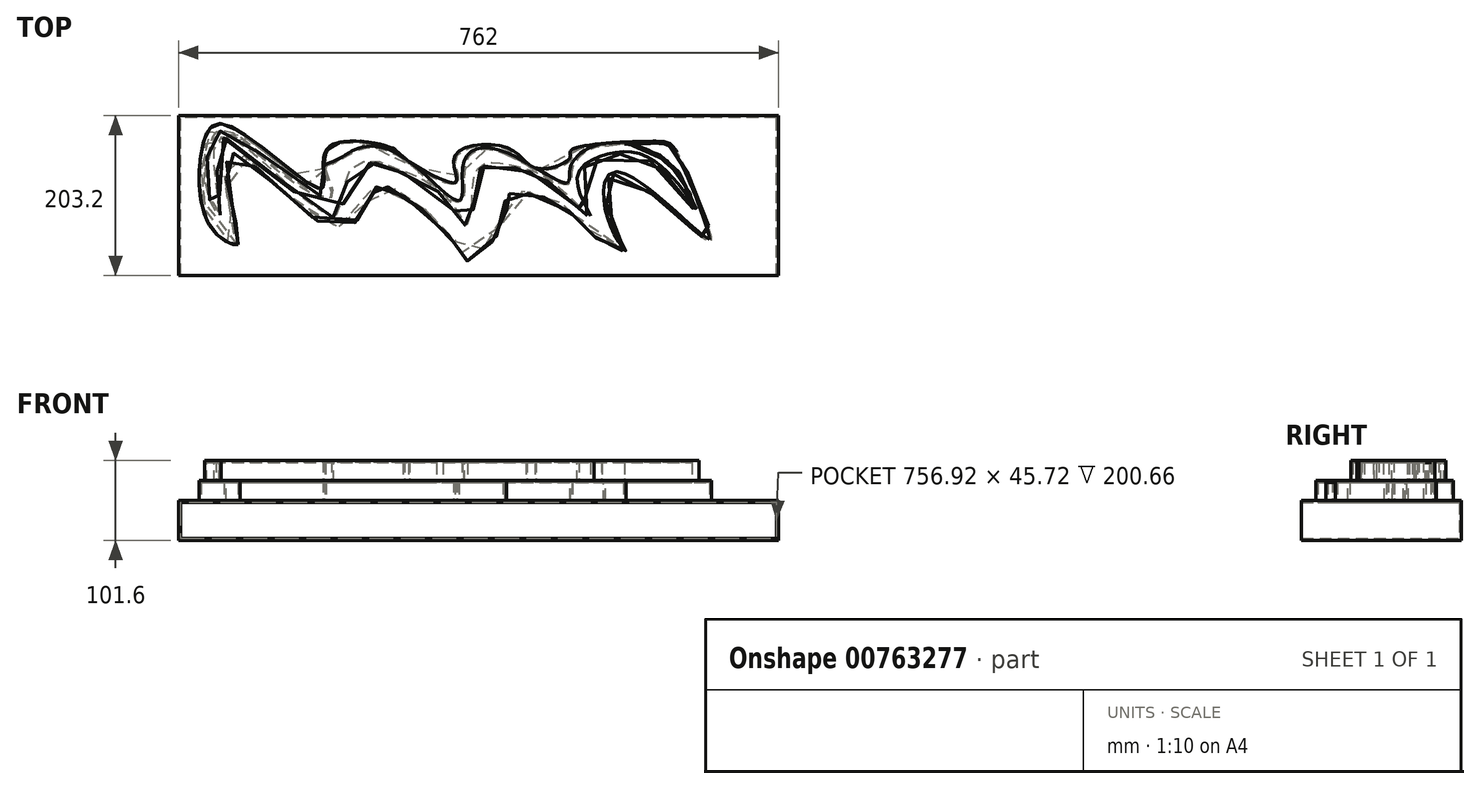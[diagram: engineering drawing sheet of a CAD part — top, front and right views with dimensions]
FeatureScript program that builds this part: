
annotation { "Feature Type Name" : "Feature", "Feature Type Description" : "" }
export const myFeature = defineFeature(function(context is Context, id is Id, definition is map)
    precondition{}
    {
        {
            var Q0;
            Q0=qCreatedBy(makeId("Front.planeOp"),FACE);
            var sketch = newSketch(context, id + "F0", { "sketchPlane" : qUnion([Q0])});
            skLineSegment(sketch, "E0.bottom", {"start": v(435.44, 50.8) * mm, "end": v(-326.56, 50.8) * mm});
            skLineSegment(sketch, "E0.top", {"start": v(435.44, 0) * mm, "end": v(-326.56, 0) * mm});
            skLineSegment(sketch, "E0.left", {"start": v(435.44, 50.8) * mm, "end": v(435.44, 0) * mm});
            skLineSegment(sketch, "E0.right", {"start": v(-326.56, 50.8) * mm, "end": v(-326.56, 0) * mm});
            skSolve(sketch);
        }
        {
            var Q0;
            Q0=makeQuery(id+"F0.imprint","IMPRINT",FACE,{"disambiguationData":[TD([[makeQuery(id+"F0.imprint","IMPRINT",EDGE,{"derivedFrom":sQuery(id+"F0.wireOp",EDGE,"E0.bottom")}),1.0]])]});
            extrude(context, id + "F1", {"entities" : qUnion([Q0]), "depth" : 203.2 * mm, "offsetDistance" : 25.4 * mm});
        }
        {
            var Q0;
            Q0=makeQuery(id+"F1.opExtrude","SWEPT_FACE",FACE,{"disambiguationData":[OSD([sQuery(id+"F0.wireOp",EDGE,"E0.bottom")])]});
            var sketch = newSketch(context, id + "F2", { "sketchPlane" : qUnion([Q0])});
            skFitSpline(sketch, "E1", {"points": [v(-250.77, -163.82) * mm, v(-255.18, -132) * mm, v(-258.15, -47.84) * mm, v(-124.06, -144.34) * mm, v(-77.46, -94.9) * mm, v(-66.59, -88.61) * mm, v(19.98, -156.73) * mm, v(42.07, -184.77) * mm, v(89.1, -128.63) * mm, v(89.96, -101.3) * mm, v(153.83, -110.58) * mm, v(200.1, -152.58) * mm, v(241.23, -171.78) * mm, v(224.31, -139.68) * mm, v(228.69, -73.8) * mm, v(347.16, -160) * mm, v(348.49, -147.43) * mm, v(304.78, -43.83) * mm, v(277.46, -32.77) * mm, v(171.93, -44.3) * mm, v(170.42, -53.77) * mm, v(128.73, -67.1) * mm, v(91.77, -41.2) * mm, v(23.32, -52.81) * mm, v(25.65, -84.74) * mm, v(-39.93, -53.9) * mm, v(-56.54, -40.94) * mm, v(-138.46, -43.15) * mm, v(-144.64, -92.88) * mm, v(-267.42, -11.32) * mm, v(-296.19, -38.66) * mm, v(-285.8, -142.18) * mm, v(-250.77, -163.82) * mm]});
            skSolve(sketch);
        }
        {
            var Q0;
            Q0=makeQuery(id+"F2.imprint","IMPRINT",FACE,{"disambiguationData":[TD([[makeQuery(id+"F2.imprint","IMPRINT",EDGE,{"derivedFrom":sQuery(id+"F2.wireOp",EDGE,"E1")}),1.0]])]});
            extrude(context, id + "F3", {"entities" : qUnion([Q0]), "operationType" : NewBodyOperationType.ADD, "depth" : 25.4 * mm, "offsetDistance" : 25.4 * mm});
        }
        {
            var Q0;
            Q0=makeQuery(id+"F3.opExtrude","CAP_FACE",FACE,{"disambiguationData":[OSD([sQuery(id+"F2.wireOp",EDGE,"E1")])],"isStart":false});
            var sketch = newSketch(context, id + "F4", { "sketchPlane" : qUnion([Q0])});
            skFitSpline(sketch, "E2", {"points": [v(-273.64, -126.3) * mm, v(-278.73, -43.22) * mm, v(-260.7, -30.87) * mm, v(-127.55, -129.53) * mm, v(-107.33, -70.92) * mm, v(-69.71, -61.74) * mm, v(-55.65, -67.6) * mm, v(6.06, -99.74) * mm, v(40.46, -140.71) * mm, v(48.82, -103.91) * mm, v(58.82, -65.47) * mm, v(104.04, -67.18) * mm, v(150.79, -90.11) * mm, v(200.7, -132.64) * mm, v(182.06, -84.44) * mm, v(204.26, -56.55) * mm, v(265.44, -53.69) * mm, v(325.36, -116.07) * mm, v(334.27, -129.9) * mm, v(314.92, -81) * mm, v(299.8, -63.41) * mm, v(273.46, -42.82) * mm, v(210.57, -35.77) * mm, v(171.23, -65.4) * mm, v(166.74, -85.54) * mm, v(81.7, -44.01) * mm, v(36.08, -58.34) * mm, v(30.62, -107.89) * mm, v(-39.77, -54.03) * mm, v(-98, -41.67) * mm, v(-130.45, -58.48) * mm, v(-142.84, -66.5) * mm, v(-132.52, -103.22) * mm, v(-200.43, -67.32) * mm, v(-257.08, -23) * mm, v(-280.25, -21.99) * mm, v(-286.25, -36.52) * mm, v(-293.04, -67.49) * mm, v(-286.52, -109.32) * mm, v(-273.64, -126.3) * mm]});
            skSolve(sketch);
        }
        {
            var Q0;
            {var subQ0=sQuery(id+"F4.wireOp",EDGE,"E2");var subQ1=makeQuery(id+"F3.opExtrude","CAP_EDGE",EDGE,{"disambiguationData":[OSD([sQuery(id+"F2.wireOp",EDGE,"E1")])],"isStart":false});var subQ8=makeQuery(id+"F4.imprint","INTERSECT",VERTEX,{"disambiguationData":[OD(0.0)],"derivedFrom":[subQ1,subQ0]});Q0=makeQuery(id+"F4.imprint","IMPRINT",FACE,{"disambiguationData":[TD([[makeQuery(id+"F4.imprint","IMPRINT",EDGE,{"disambiguationData":[TD([[subQ8,-1.0]])],"derivedFrom":subQ0}),1.0]])]});}
            extrude(context, id + "F5", {"entities" : qUnion([Q0]), "operationType" : NewBodyOperationType.ADD, "depth" : 25.4 * mm, "offsetDistance" : 25.4 * mm});
        }
        {
            var Q0;
            Q0=makeQuery(id+"F1.opExtrude","CAP_FACE",FACE,{"disambiguationData":[OSD([sQuery(id+"F0.wireOp",EDGE,"E0.bottom"),sQuery(id+"F0.wireOp",EDGE,"E0.top"),sQuery(id+"F0.wireOp",EDGE,"E0.left"),sQuery(id+"F0.wireOp",EDGE,"E0.right")])],"isStart":false});
            shell(context, id + "F6", {"entities" : qUnion([Q0]), "thickness" : 2.54 * mm});
        }
    });
